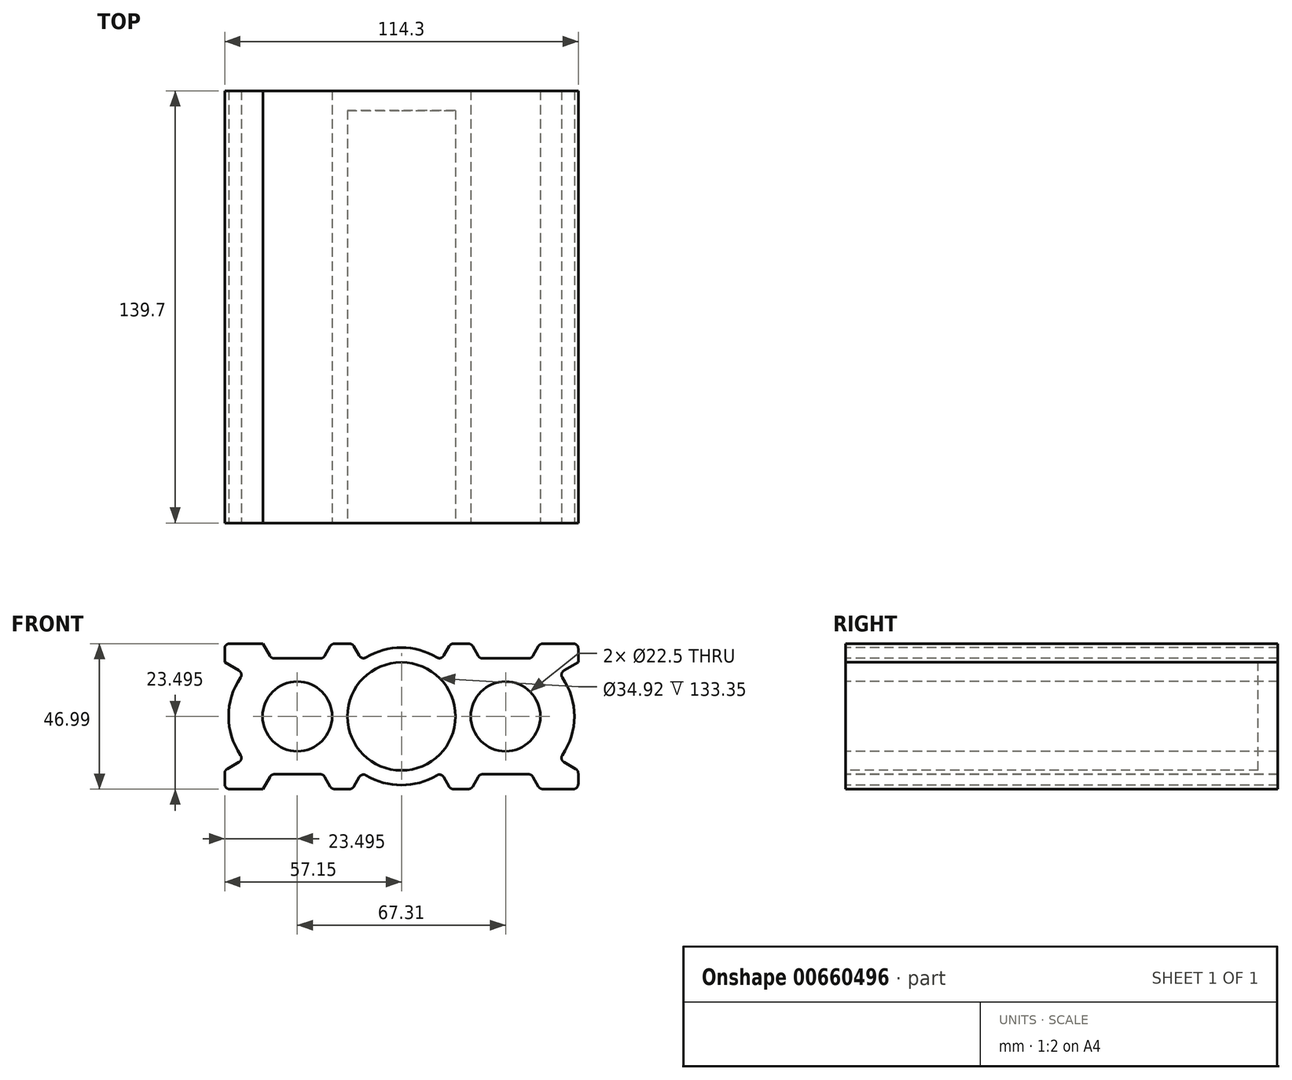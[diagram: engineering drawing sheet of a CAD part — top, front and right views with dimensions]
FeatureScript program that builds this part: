
annotation { "Feature Type Name" : "Feature", "Feature Type Description" : "" }
export const myFeature = defineFeature(function(context is Context, id is Id, definition is map)
    precondition{}
    {
        {
            var Q0;
            Q0=qCreatedBy(makeId("Top.planeOp"),FACE);
            var sketch = newSketch(context, id + "F0", { "sketchPlane" : qUnion([Q0])});
            skLineSegment(sketch, "E0.bottom", {"start": v(57.15, 69.85) * mm, "end": v(-57.15, 69.85) * mm});
            skLineSegment(sketch, "E0.top", {"start": v(57.15, -69.85) * mm, "end": v(-57.15, -69.85) * mm});
            skLineSegment(sketch, "E0.left", {"start": v(57.15, 69.85) * mm, "end": v(57.15, -69.85) * mm});
            skLineSegment(sketch, "E0.right", {"start": v(-57.15, 69.85) * mm, "end": v(-57.15, -69.85) * mm});
            skPoint(sketch, "E0.middle", {"position": v(0, 0) * mm});
            skSolve(sketch);
        }
        {
            var Q0;
            Q0 = qSketchRegion(id + "F0", true);
            extrude(context, id + "F1", {"entities" : qUnion([Q0]), "depth" : 47 * mm, "offsetDistance" : 25.4 * mm});
        }
        {
            var Q0;
            Q0=makeQuery(id+"F1.opExtrude","SWEPT_FACE",FACE,{"disambiguationData":[OSD([sQuery(id+"F0.wireOp",EDGE,"E0.top")])]});
            var sketch = newSketch(context, id + "F2", { "sketchPlane" : qUnion([Q0])});
            skPoint(sketch, "E1", {"position": v(-33.65, 23.5) * mm});
            skLineSegment(sketch, "E2", {"start": v(-33.65, 23.5) * mm, "end": v(-57.15, 23.5) * mm, "construction": true});
            skLineSegment(sketch, "E3", {"start": v(-33.65, 23.5) * mm, "end": v(-33.65, 47) * mm, "construction": true});
            skLineSegment(sketch, "E4", {"start": v(-33.65, 23.5) * mm, "end": v(-33.65, 0) * mm, "construction": true});
            skPoint(sketch, "E5.MirrorP", {"position": v(33.65, 23.5) * mm});
            skSolve(sketch);
        }
        {
            var Q0;
            Q0=sQuery(id+"F2.wireOp",VERTEX,"E1");
            var Q1;
            Q1=sQuery(id+"F2.wireOp",VERTEX,"E5.MirrorP");
            var Q2;
            Q2=makeQuery(id+"F1.opExtrude","SWEPT_BODY",BODY,{"disambiguationData":[OSD([sQuery(id+"F0.wireOp",EDGE,"E0.bottom"),sQuery(id+"F0.wireOp",EDGE,"E0.top"),sQuery(id+"F0.wireOp",EDGE,"E0.left"),sQuery(id+"F0.wireOp",EDGE,"E0.right")])]});
            hole(context, id + "F3", {"style" : HoleStyle.SIMPLE, "endStyle" : HoleEndStyle.THROUGH, "holeDiameter" : 22.5 * mm, "majorDiameter" : 6.35 * mm, "isTappedThrough" : true, "tappedDepth" : 12.7 * mm, "tapClearance" : 3, "locations" : qUnion([Q0, Q1]), "scope" : qUnion([Q2])});
        }
        {
            var Q0;
            Q0=makeQuery(id+"F1.opExtrude","SWEPT_FACE",FACE,{"disambiguationData":[OSD([sQuery(id+"F0.wireOp",EDGE,"E0.top")])]});
            var sketch = newSketch(context, id + "F4", { "sketchPlane" : qUnion([Q0])});
            skPoint(sketch, "E6", {"position": v(0, 23.5) * mm});
            skLineSegment(sketch, "E7", {"start": v(0, 47) * mm, "end": v(0, 0) * mm, "construction": true});
            skCircle(sketch, "E8", {"center": v(0, 23.5) * mm, "radius": 17.46 * mm});
            skSolve(sketch);
        }
        {
            var Q0;
            Q0=makeQuery(id+"F4.imprint","IMPRINT",FACE,{"disambiguationData":[TD([[makeQuery(id+"F4.imprint","IMPRINT",EDGE,{"derivedFrom":sQuery(id+"F4.wireOp",EDGE,"E8")}),1.0]])]});
            extrude(context, id + "F5", {"entities" : qUnion([Q0]), "operationType" : NewBodyOperationType.REMOVE, "endBound" : BoundingType.UP_TO_NEXT, "oppositeDirection" : true, "depth" : 25.4 * mm, "hasOffset" : true, "offsetDistance" : 6.35 * mm});
        }
        {
            var Q0;
            Q0=makeQuery(id+"F1.opExtrude","SWEPT_FACE",FACE,{"disambiguationData":[OSD([sQuery(id+"F0.wireOp",EDGE,"E0.top")])]});
            var sketch = newSketch(context, id + "F6", { "sketchPlane" : qUnion([Q0])});
            skLineSegment(sketch, "E9", {"start": v(-57.15, 40.96) * mm, "end": v(-51, 37.4) * mm});
            skLineSegment(sketch, "E10", {"start": v(-51, 9.59) * mm, "end": v(-57.15, 6.03) * mm});
            skLineSegment(sketch, "E11", {"start": v(-57.15, 6.03) * mm, "end": v(-57.15, 40.96) * mm});
            skArc(sketch, "E12", {"start": v(-51, 37.4) * mm, "mid": v(-55.88, 23.5) * mm, "end": v(-51, 9.59) * mm});
            skLineSegment(sketch, "E13", {"start": v(-57.15, 47) * mm, "end": v(-57.15, 40.96) * mm, "construction": true});
            skLineSegment(sketch, "E14", {"start": v(-57.15, 0) * mm, "end": v(-57.15, 6.03) * mm, "construction": true});
            skLineSegment(sketch, "E15", {"start": v(-44.77, 46.99) * mm, "end": v(-42.02, 42.23) * mm});
            skLineSegment(sketch, "E16", {"start": v(-42.02, 42.23) * mm, "end": v(-25.3, 42.23) * mm});
            skLineSegment(sketch, "E17", {"start": v(-25.3, 42.23) * mm, "end": v(-22.54, 47) * mm});
            skLineSegment(sketch, "E18", {"start": v(-44.77, 47) * mm, "end": v(-22.54, 47) * mm});
            skLineSegment(sketch, "E19", {"start": v(-15.88, 47) * mm, "end": v(-12.8, 41.66) * mm});
            skLineSegment(sketch, "E20", {"start": v(15.88, 47) * mm, "end": v(12.8, 41.66) * mm});
            skLineSegment(sketch, "E21", {"start": v(-15.88, 47) * mm, "end": v(15.88, 47) * mm});
            skArc(sketch, "E22", {"start": v(12.8, 41.66) * mm, "mid": v(0, 45.72) * mm, "end": v(-12.8, 41.66) * mm});
            skLineSegment(sketch, "E23", {"start": v(-33.65, 42.23) * mm, "end": v(-33.65, 23.5) * mm, "construction": true});
            skLineSegment(sketch, "E24", {"start": v(0, 47) * mm, "end": v(0, 23.5) * mm, "construction": true});
            skLineSegment(sketch, "E25", {"start": v(-33.65, 23.5) * mm, "end": v(0, 23.5) * mm, "construction": true});
            skLineSegment(sketch, "E26.MirrorCS", {"start": v(44.77, 47) * mm, "end": v(42.02, 42.23) * mm});
            skLineSegment(sketch, "E27.MirrorCS", {"start": v(44.77, 47) * mm, "end": v(22.54, 47) * mm});
            skLineSegment(sketch, "E28.MirrorCS", {"start": v(42.02, 42.23) * mm, "end": v(25.3, 42.23) * mm});
            skLineSegment(sketch, "E29.MirrorCS", {"start": v(25.3, 42.23) * mm, "end": v(22.54, 47) * mm});
            skLineSegment(sketch, "E30.MirrorCS", {"start": v(57.15, 40.96) * mm, "end": v(51, 37.4) * mm});
            skLineSegment(sketch, "E31.MirrorCS", {"start": v(57.15, 6.03) * mm, "end": v(57.15, 40.96) * mm});
            skArc(sketch, "E32.MirrorCS", {"start": v(51, 37.4) * mm, "mid": v(55.88, 23.5) * mm, "end": v(51, 9.59) * mm});
            skLineSegment(sketch, "E33.MirrorCS", {"start": v(51, 9.59) * mm, "end": v(57.15, 6.03) * mm});
            skLineSegment(sketch, "E34.MirrorCS", {"start": v(-42.02, 4.76) * mm, "end": v(-25.3, 4.76) * mm});
            skLineSegment(sketch, "E35.MirrorCS", {"start": v(-44.77, 0) * mm, "end": v(-42.02, 4.76) * mm});
            skLineSegment(sketch, "E36.MirrorCS", {"start": v(-44.77, 0) * mm, "end": v(-22.54, 0) * mm});
            skLineSegment(sketch, "E37.MirrorCS", {"start": v(-25.3, 4.76) * mm, "end": v(-22.54, 0) * mm});
            skLineSegment(sketch, "E38.MirrorCS", {"start": v(-15.88, 0) * mm, "end": v(-12.8, 5.33) * mm});
            skArc(sketch, "E39.MirrorCS", {"start": v(12.8, 5.33) * mm, "mid": v(0, 1.27) * mm, "end": v(-12.8, 5.33) * mm});
            skLineSegment(sketch, "E40.MirrorCS", {"start": v(-15.88, 0) * mm, "end": v(15.88, 0) * mm});
            skLineSegment(sketch, "E41.MirrorCS", {"start": v(15.88, 0) * mm, "end": v(12.8, 5.33) * mm});
            skLineSegment(sketch, "E42.MirrorCS", {"start": v(25.3, 4.76) * mm, "end": v(22.54, 0) * mm});
            skLineSegment(sketch, "E43.MirrorCS", {"start": v(44.77, 0) * mm, "end": v(22.54, 0) * mm});
            skLineSegment(sketch, "E44.MirrorCS", {"start": v(42.02, 4.76) * mm, "end": v(25.3, 4.76) * mm});
            skLineSegment(sketch, "E45.MirrorCS", {"start": v(44.77, 0) * mm, "end": v(42.02, 4.76) * mm});
            skSolve(sketch);
        }
        {
            var Q0;
            Q0=makeQuery(id+"F6.imprint","IMPRINT",FACE,{"disambiguationData":[TD([[makeQuery(id+"F6.imprint","IMPRINT",EDGE,{"derivedFrom":sQuery(id+"F6.wireOp",EDGE,"E9")}),-1.0]])]});
            var Q1;
            Q1=makeQuery(id+"F6.imprint","IMPRINT",FACE,{"disambiguationData":[TD([[makeQuery(id+"F6.imprint","IMPRINT",EDGE,{"derivedFrom":sQuery(id+"F6.wireOp",EDGE,"E15")}),1.0]])]});
            var Q2;
            Q2=makeQuery(id+"F6.imprint","IMPRINT",FACE,{"disambiguationData":[TD([[makeQuery(id+"F6.imprint","IMPRINT",EDGE,{"derivedFrom":sQuery(id+"F6.wireOp",EDGE,"E34.MirrorCS")}),-1.0]])]});
            var Q3;
            Q3=makeQuery(id+"F6.imprint","IMPRINT",FACE,{"disambiguationData":[TD([[makeQuery(id+"F6.imprint","IMPRINT",EDGE,{"derivedFrom":sQuery(id+"F6.wireOp",EDGE,"E38.MirrorCS")}),-1.0]])]});
            var Q4;
            Q4=makeQuery(id+"F6.imprint","IMPRINT",FACE,{"disambiguationData":[TD([[makeQuery(id+"F6.imprint","IMPRINT",EDGE,{"derivedFrom":sQuery(id+"F6.wireOp",EDGE,"E19")}),1.0]])]});
            var Q5;
            Q5=makeQuery(id+"F6.imprint","IMPRINT",FACE,{"disambiguationData":[TD([[makeQuery(id+"F6.imprint","IMPRINT",EDGE,{"derivedFrom":sQuery(id+"F6.wireOp",EDGE,"E26.MirrorCS")}),-1.0]])]});
            var Q6;
            Q6=makeQuery(id+"F6.imprint","IMPRINT",FACE,{"disambiguationData":[TD([[makeQuery(id+"F6.imprint","IMPRINT",EDGE,{"derivedFrom":sQuery(id+"F6.wireOp",EDGE,"E42.MirrorCS")}),1.0]])]});
            var Q7;
            Q7=makeQuery(id+"F6.imprint","IMPRINT",FACE,{"disambiguationData":[TD([[makeQuery(id+"F6.imprint","IMPRINT",EDGE,{"derivedFrom":sQuery(id+"F6.wireOp",EDGE,"E30.MirrorCS")}),1.0]])]});
            extrude(context, id + "F7", {"entities" : qUnion([Q0, Q1, Q2, Q3, Q4, Q5, Q6, Q7]), "operationType" : NewBodyOperationType.REMOVE, "endBound" : BoundingType.THROUGH_ALL, "oppositeDirection" : true, "depth" : 25.4 * mm, "offsetDistance" : 25.4 * mm});
        }
        {
            var Q0;
            Q0=makeQuery(id+"F1.opExtrude","CAP_EDGE",EDGE,{"disambiguationData":[OSD([sQuery(id+"F0.wireOp",EDGE,"E0.right")])],"isStart":true});
            var Q1;
            Q1=makeQuery(id+"F7.boolean.opBoolean","COPY",EDGE,{"derivedFrom":makeQuery(id+"F7.opExtrude","SWEPT_EDGE",EDGE,{"disambiguationData":[OSD([sQuery(id+"F0.wireOp",EDGE,"E0.top"),sQuery(id+"F6.wireOp",EDGE,"E35.MirrorCS"),sQuery(id+"F6.wireOp",EDGE,"E36.MirrorCS")])]})});
            var Q2;
            Q2=makeQuery(id+"F7.boolean.opBoolean","COPY",EDGE,{"derivedFrom":makeQuery(id+"F7.opExtrude","SWEPT_EDGE",EDGE,{"disambiguationData":[OSD([sQuery(id+"F6.wireOp",EDGE,"E34.MirrorCS"),sQuery(id+"F6.wireOp",EDGE,"E35.MirrorCS")])]})});
            var Q3;
            Q3=makeQuery(id+"F7.boolean.opBoolean","COPY",EDGE,{"derivedFrom":makeQuery(id+"F7.opExtrude","SWEPT_EDGE",EDGE,{"disambiguationData":[OSD([sQuery(id+"F6.wireOp",EDGE,"E34.MirrorCS"),sQuery(id+"F6.wireOp",EDGE,"E37.MirrorCS")])]})});
            var Q4;
            Q4=makeQuery(id+"F7.boolean.opBoolean","COPY",EDGE,{"derivedFrom":makeQuery(id+"F7.opExtrude","SWEPT_EDGE",EDGE,{"disambiguationData":[OSD([sQuery(id+"F0.wireOp",EDGE,"E0.top"),sQuery(id+"F6.wireOp",EDGE,"E36.MirrorCS"),sQuery(id+"F6.wireOp",EDGE,"E37.MirrorCS")])]})});
            var Q5;
            Q5=makeQuery(id+"F7.boolean.opBoolean","COPY",EDGE,{"derivedFrom":makeQuery(id+"F7.opExtrude","SWEPT_EDGE",EDGE,{"disambiguationData":[OSD([sQuery(id+"F0.wireOp",EDGE,"E0.top"),sQuery(id+"F6.wireOp",EDGE,"E38.MirrorCS"),sQuery(id+"F6.wireOp",EDGE,"E40.MirrorCS")])]})});
            var Q6;
            Q6=makeQuery(id+"F7.boolean.opBoolean","COPY",EDGE,{"derivedFrom":makeQuery(id+"F7.opExtrude","SWEPT_EDGE",EDGE,{"disambiguationData":[OSD([sQuery(id+"F6.wireOp",EDGE,"E38.MirrorCS"),sQuery(id+"F6.wireOp",EDGE,"E39.MirrorCS")])]})});
            var Q7;
            Q7=makeQuery(id+"F7.boolean.opBoolean","COPY",EDGE,{"derivedFrom":makeQuery(id+"F7.opExtrude","SWEPT_EDGE",EDGE,{"disambiguationData":[OSD([sQuery(id+"F6.wireOp",EDGE,"E39.MirrorCS"),sQuery(id+"F6.wireOp",EDGE,"E41.MirrorCS")])]})});
            var Q8;
            Q8=makeQuery(id+"F7.boolean.opBoolean","COPY",EDGE,{"derivedFrom":makeQuery(id+"F7.opExtrude","SWEPT_EDGE",EDGE,{"disambiguationData":[OSD([sQuery(id+"F0.wireOp",EDGE,"E0.top"),sQuery(id+"F6.wireOp",EDGE,"E40.MirrorCS"),sQuery(id+"F6.wireOp",EDGE,"E41.MirrorCS")])]})});
            var Q9;
            Q9=makeQuery(id+"F7.boolean.opBoolean","COPY",EDGE,{"derivedFrom":makeQuery(id+"F7.opExtrude","SWEPT_EDGE",EDGE,{"disambiguationData":[OSD([sQuery(id+"F0.wireOp",EDGE,"E0.top"),sQuery(id+"F6.wireOp",EDGE,"E42.MirrorCS"),sQuery(id+"F6.wireOp",EDGE,"E43.MirrorCS")])]})});
            var Q10;
            Q10=makeQuery(id+"F7.boolean.opBoolean","COPY",EDGE,{"derivedFrom":makeQuery(id+"F7.opExtrude","SWEPT_EDGE",EDGE,{"disambiguationData":[OSD([sQuery(id+"F6.wireOp",EDGE,"E42.MirrorCS"),sQuery(id+"F6.wireOp",EDGE,"E44.MirrorCS")])]})});
            var Q11;
            Q11=makeQuery(id+"F7.boolean.opBoolean","COPY",EDGE,{"derivedFrom":makeQuery(id+"F7.opExtrude","SWEPT_EDGE",EDGE,{"disambiguationData":[OSD([sQuery(id+"F6.wireOp",EDGE,"E44.MirrorCS"),sQuery(id+"F6.wireOp",EDGE,"E45.MirrorCS")])]})});
            var Q12;
            Q12=makeQuery(id+"F7.boolean.opBoolean","COPY",EDGE,{"derivedFrom":makeQuery(id+"F7.opExtrude","SWEPT_EDGE",EDGE,{"disambiguationData":[OSD([sQuery(id+"F0.wireOp",EDGE,"E0.top"),sQuery(id+"F6.wireOp",EDGE,"E43.MirrorCS"),sQuery(id+"F6.wireOp",EDGE,"E45.MirrorCS")])]})});
            var Q13;
            Q13=makeQuery(id+"F1.opExtrude","CAP_EDGE",EDGE,{"disambiguationData":[OSD([sQuery(id+"F0.wireOp",EDGE,"E0.left")])],"isStart":true});
            var Q14;
            Q14=makeQuery(id+"F7.boolean.opBoolean","COPY",EDGE,{"derivedFrom":makeQuery(id+"F7.opExtrude","SWEPT_EDGE",EDGE,{"disambiguationData":[OSD([sQuery(id+"F0.wireOp",EDGE,"E0.top"),sQuery(id+"F0.wireOp",EDGE,"E0.left"),sQuery(id+"F6.wireOp",EDGE,"E31.MirrorCS"),sQuery(id+"F6.wireOp",EDGE,"E33.MirrorCS")])]})});
            var Q15;
            Q15=makeQuery(id+"F7.boolean.opBoolean","COPY",EDGE,{"derivedFrom":makeQuery(id+"F7.opExtrude","SWEPT_EDGE",EDGE,{"disambiguationData":[OSD([sQuery(id+"F6.wireOp",EDGE,"E30.MirrorCS"),sQuery(id+"F6.wireOp",EDGE,"E32.MirrorCS")])]})});
            var Q16;
            Q16=makeQuery(id+"F7.boolean.opBoolean","COPY",EDGE,{"derivedFrom":makeQuery(id+"F7.opExtrude","SWEPT_EDGE",EDGE,{"disambiguationData":[OSD([sQuery(id+"F6.wireOp",EDGE,"E32.MirrorCS"),sQuery(id+"F6.wireOp",EDGE,"E33.MirrorCS")])]})});
            var Q17;
            Q17=makeQuery(id+"F1.opExtrude","CAP_EDGE",EDGE,{"disambiguationData":[OSD([sQuery(id+"F0.wireOp",EDGE,"E0.left")])],"isStart":false});
            var Q18;
            Q18=makeQuery(id+"F7.boolean.opBoolean","COPY",EDGE,{"derivedFrom":makeQuery(id+"F7.opExtrude","SWEPT_EDGE",EDGE,{"disambiguationData":[OSD([sQuery(id+"F0.wireOp",EDGE,"E0.top"),sQuery(id+"F6.wireOp",EDGE,"E26.MirrorCS"),sQuery(id+"F6.wireOp",EDGE,"E27.MirrorCS")])]})});
            var Q19;
            Q19=makeQuery(id+"F7.boolean.opBoolean","COPY",EDGE,{"derivedFrom":makeQuery(id+"F7.opExtrude","SWEPT_EDGE",EDGE,{"disambiguationData":[OSD([sQuery(id+"F6.wireOp",EDGE,"E26.MirrorCS"),sQuery(id+"F6.wireOp",EDGE,"E28.MirrorCS")])]})});
            var Q20;
            Q20=makeQuery(id+"F7.boolean.opBoolean","COPY",EDGE,{"derivedFrom":makeQuery(id+"F7.opExtrude","SWEPT_EDGE",EDGE,{"disambiguationData":[OSD([sQuery(id+"F6.wireOp",EDGE,"E28.MirrorCS"),sQuery(id+"F6.wireOp",EDGE,"E29.MirrorCS")])]})});
            var Q21;
            Q21=makeQuery(id+"F7.boolean.opBoolean","COPY",EDGE,{"derivedFrom":makeQuery(id+"F7.opExtrude","SWEPT_EDGE",EDGE,{"disambiguationData":[OSD([sQuery(id+"F0.wireOp",EDGE,"E0.top"),sQuery(id+"F6.wireOp",EDGE,"E27.MirrorCS"),sQuery(id+"F6.wireOp",EDGE,"E29.MirrorCS")])]})});
            var Q22;
            Q22=makeQuery(id+"F7.boolean.opBoolean","COPY",EDGE,{"derivedFrom":makeQuery(id+"F7.opExtrude","SWEPT_EDGE",EDGE,{"disambiguationData":[OSD([sQuery(id+"F0.wireOp",EDGE,"E0.top"),sQuery(id+"F6.wireOp",EDGE,"E20"),sQuery(id+"F6.wireOp",EDGE,"E21")])]})});
            var Q23;
            Q23=makeQuery(id+"F7.boolean.opBoolean","COPY",EDGE,{"derivedFrom":makeQuery(id+"F7.opExtrude","SWEPT_EDGE",EDGE,{"disambiguationData":[OSD([sQuery(id+"F6.wireOp",EDGE,"E20"),sQuery(id+"F6.wireOp",EDGE,"E22")])]})});
            var Q24;
            Q24=makeQuery(id+"F7.boolean.opBoolean","COPY",EDGE,{"derivedFrom":makeQuery(id+"F7.opExtrude","SWEPT_EDGE",EDGE,{"disambiguationData":[OSD([sQuery(id+"F6.wireOp",EDGE,"E19"),sQuery(id+"F6.wireOp",EDGE,"E22")])]})});
            var Q25;
            Q25=makeQuery(id+"F7.boolean.opBoolean","COPY",EDGE,{"derivedFrom":makeQuery(id+"F7.opExtrude","SWEPT_EDGE",EDGE,{"disambiguationData":[OSD([sQuery(id+"F0.wireOp",EDGE,"E0.top"),sQuery(id+"F6.wireOp",EDGE,"E19"),sQuery(id+"F6.wireOp",EDGE,"E21")])]})});
            var Q26;
            Q26=makeQuery(id+"F7.boolean.opBoolean","COPY",EDGE,{"derivedFrom":makeQuery(id+"F7.opExtrude","SWEPT_EDGE",EDGE,{"disambiguationData":[OSD([sQuery(id+"F0.wireOp",EDGE,"E0.top"),sQuery(id+"F6.wireOp",EDGE,"E17"),sQuery(id+"F6.wireOp",EDGE,"E18")])]})});
            var Q27;
            Q27=makeQuery(id+"F7.boolean.opBoolean","COPY",EDGE,{"derivedFrom":makeQuery(id+"F7.opExtrude","SWEPT_EDGE",EDGE,{"disambiguationData":[OSD([sQuery(id+"F6.wireOp",EDGE,"E16"),sQuery(id+"F6.wireOp",EDGE,"E17")])]})});
            var Q28;
            Q28=makeQuery(id+"F7.boolean.opBoolean","COPY",EDGE,{"derivedFrom":makeQuery(id+"F7.opExtrude","SWEPT_EDGE",EDGE,{"disambiguationData":[OSD([sQuery(id+"F6.wireOp",EDGE,"E15"),sQuery(id+"F6.wireOp",EDGE,"E16")])]})});
            var Q29;
            Q29=makeQuery(id+"F7.boolean.opBoolean","COPY",EDGE,{"derivedFrom":makeQuery(id+"F7.opExtrude","SWEPT_EDGE",EDGE,{"disambiguationData":[OSD([sQuery(id+"F0.wireOp",EDGE,"E0.top"),sQuery(id+"F6.wireOp",EDGE,"E15"),sQuery(id+"F6.wireOp",EDGE,"E18")])]})});
            var Q30;
            Q30=makeQuery(id+"F1.opExtrude","CAP_EDGE",EDGE,{"disambiguationData":[OSD([sQuery(id+"F0.wireOp",EDGE,"E0.right")])],"isStart":false});
            var Q31;
            Q31=makeQuery(id+"F7.boolean.opBoolean","COPY",EDGE,{"derivedFrom":makeQuery(id+"F7.opExtrude","SWEPT_EDGE",EDGE,{"disambiguationData":[OSD([sQuery(id+"F0.wireOp",EDGE,"E0.top"),sQuery(id+"F0.wireOp",EDGE,"E0.right"),sQuery(id+"F6.wireOp",EDGE,"E9"),sQuery(id+"F6.wireOp",EDGE,"E11")])]})});
            var Q32;
            Q32=makeQuery(id+"F7.boolean.opBoolean","COPY",EDGE,{"derivedFrom":makeQuery(id+"F7.opExtrude","SWEPT_EDGE",EDGE,{"disambiguationData":[OSD([sQuery(id+"F6.wireOp",EDGE,"E9"),sQuery(id+"F6.wireOp",EDGE,"E12")])]})});
            var Q33;
            Q33=makeQuery(id+"F7.boolean.opBoolean","COPY",EDGE,{"derivedFrom":makeQuery(id+"F7.opExtrude","SWEPT_EDGE",EDGE,{"disambiguationData":[OSD([sQuery(id+"F6.wireOp",EDGE,"E10"),sQuery(id+"F6.wireOp",EDGE,"E12")])]})});
            var Q34;
            Q34=makeQuery(id+"F7.boolean.opBoolean","COPY",EDGE,{"derivedFrom":makeQuery(id+"F7.opExtrude","SWEPT_EDGE",EDGE,{"disambiguationData":[OSD([sQuery(id+"F0.wireOp",EDGE,"E0.top"),sQuery(id+"F0.wireOp",EDGE,"E0.right"),sQuery(id+"F6.wireOp",EDGE,"E10"),sQuery(id+"F6.wireOp",EDGE,"E11")])]})});
            fillet(context, id + "F8", {"entities" : qUnion([Q0, Q1, Q2, Q3, Q4, Q5, Q6, Q7, Q8, Q9, Q10, Q11, Q12, Q13, Q14, Q15, Q16, Q17, Q18, Q19, Q20, Q21, Q22, Q23, Q24, Q25, Q26, Q27, Q28, Q29, Q30, Q31, Q32, Q33, Q34]), "radius" : 1.59 * mm, "tangentPropagation" : true, "allowEdgeOverflow" : false});
        }
    });
